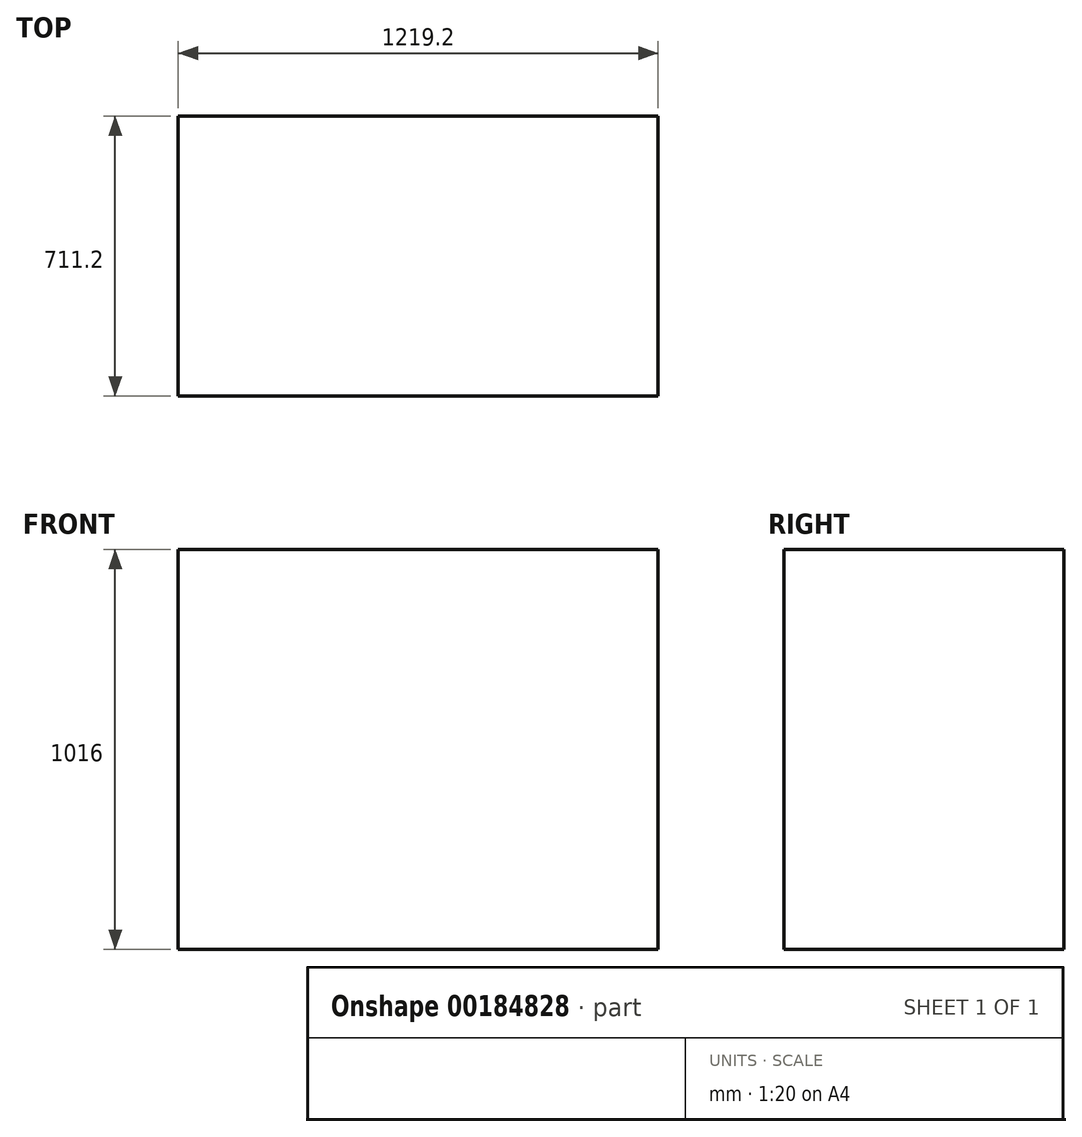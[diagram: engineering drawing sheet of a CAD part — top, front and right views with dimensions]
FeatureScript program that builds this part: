
annotation { "Feature Type Name" : "Feature", "Feature Type Description" : "" }
export const myFeature = defineFeature(function(context is Context, id is Id, definition is map)
    precondition{}
    {
        {
            var Q0;
            Q0=qCreatedBy(makeId("Top.planeOp"),FACE);
            var sketch = newSketch(context, id + "F0", { "sketchPlane" : qUnion([Q0])});
            skLineSegment(sketch, "E0.bottom", {"start": v(609.6, -355.6) * mm, "end": v(-609.6, -355.6) * mm});
            skLineSegment(sketch, "E0.top", {"start": v(609.6, 355.6) * mm, "end": v(-609.6, 355.6) * mm});
            skLineSegment(sketch, "E0.left", {"start": v(609.6, -355.6) * mm, "end": v(609.6, 355.6) * mm});
            skLineSegment(sketch, "E0.right", {"start": v(-609.6, -355.6) * mm, "end": v(-609.6, 355.6) * mm});
            skPoint(sketch, "E0.middle", {"position": v(0, 0) * mm});
            skSolve(sketch);
        }
        {
            var Q0;
            Q0=makeQuery(id+"F0.imprint","IMPRINT",FACE,{"disambiguationData":[TD([[makeQuery(id+"F0.imprint","IMPRINT",EDGE,{"derivedFrom":sQuery(id+"F0.wireOp",EDGE,"E0.bottom")}),-1.0]])]});
            extrude(context, id + "F1", {"entities" : qUnion([Q0]), "depth" : 1016 * mm});
        }
    });
